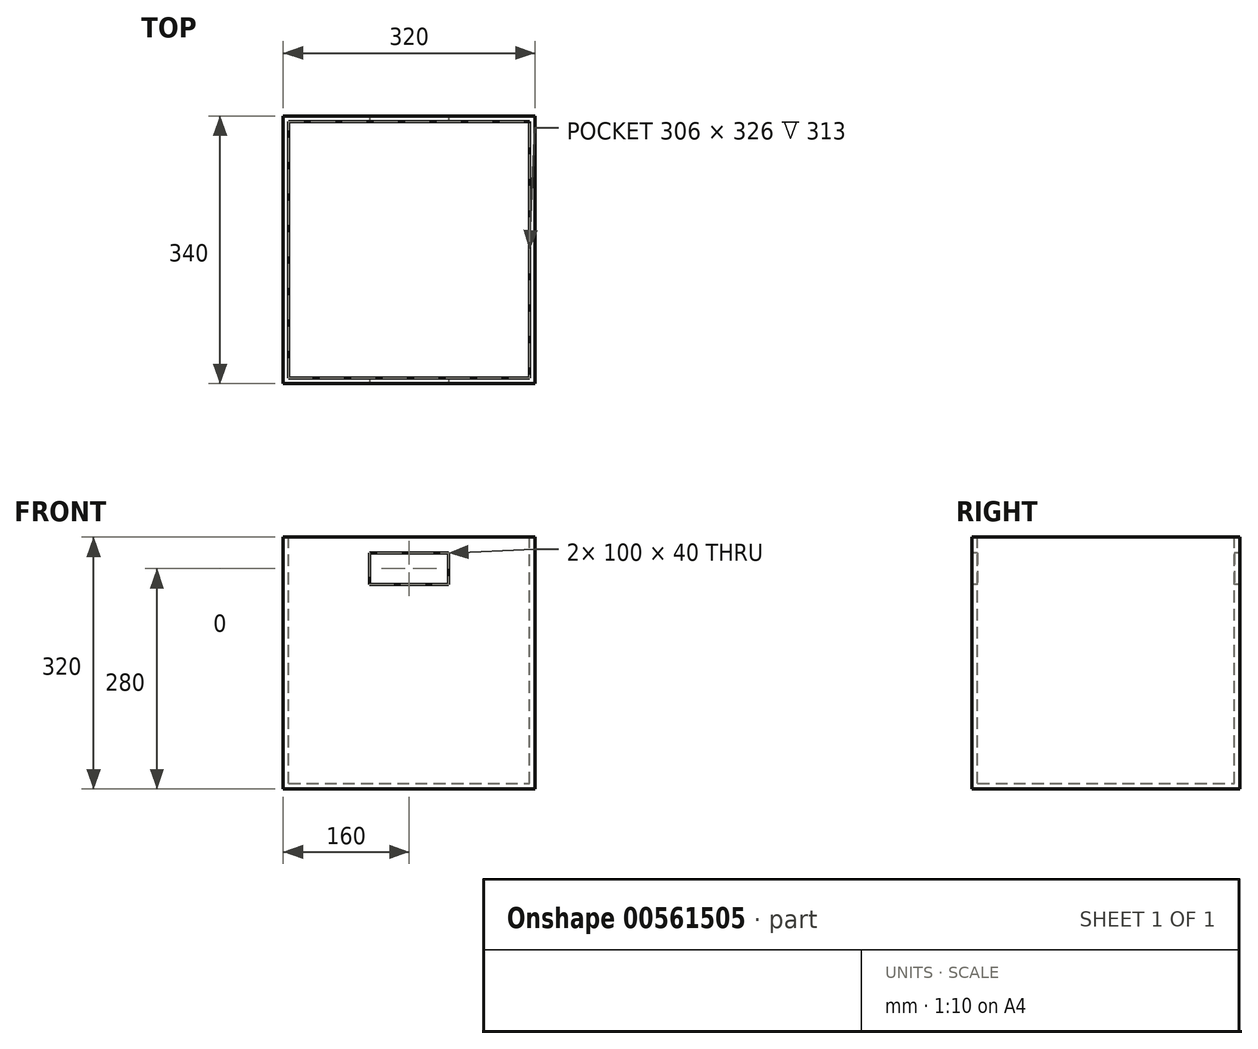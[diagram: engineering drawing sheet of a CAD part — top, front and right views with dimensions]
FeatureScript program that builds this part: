
annotation { "Feature Type Name" : "Feature", "Feature Type Description" : "" }
export const myFeature = defineFeature(function(context is Context, id is Id, definition is map)
    precondition{}
    {
        {
            var Q0;
            Q0=qCreatedBy(makeId("Front.planeOp"),FACE);
            var sketch = newSketch(context, id + "F0", { "sketchPlane" : qUnion([Q0])});
            skLineSegment(sketch, "E0.bottom", {"start": v(0, 0) * mm, "end": v(320, 0) * mm});
            skLineSegment(sketch, "E0.top", {"start": v(0, 320) * mm, "end": v(320, 320) * mm});
            skLineSegment(sketch, "E0.left", {"start": v(0, 0) * mm, "end": v(0, 320) * mm});
            skLineSegment(sketch, "E0.right", {"start": v(320, 0) * mm, "end": v(320, 320) * mm});
            skSolve(sketch);
        }
        {
            var Q0;
            Q0 = qSketchRegion(id + "F0", true);
            extrude(context, id + "F1", {"entities" : qUnion([Q0]), "depth" : 340 * mm, "offsetDistance" : 25 * mm, "symmetric" : true});
        }
        {
            var Q0;
            Q0=makeQuery(id+"F1.opExtrude","SWEPT_FACE",FACE,{"disambiguationData":[OSD([sQuery(id+"F0.wireOp",EDGE,"E0.top")])]});
            shell(context, id + "F2", {"entities" : qUnion([Q0]), "thickness" : 7 * mm});
        }
        {
            var Q0;
            Q0=makeQuery(id+"F1.opExtrude","CAP_FACE",FACE,{"disambiguationData":[OSD([sQuery(id+"F0.wireOp",EDGE,"E0.bottom"),sQuery(id+"F0.wireOp",EDGE,"E0.top"),sQuery(id+"F0.wireOp",EDGE,"E0.left"),sQuery(id+"F0.wireOp",EDGE,"E0.right")])],"isStart":false});
            var sketch = newSketch(context, id + "F3", { "sketchPlane" : qUnion([Q0])});
            skLineSegment(sketch, "E1.bottom", {"start": v(110, 300) * mm, "end": v(210, 300) * mm});
            skLineSegment(sketch, "E1.top", {"start": v(110, 260) * mm, "end": v(210, 260) * mm});
            skLineSegment(sketch, "E1.left", {"start": v(110, 300) * mm, "end": v(110, 260) * mm});
            skLineSegment(sketch, "E1.right", {"start": v(210, 300) * mm, "end": v(210, 260) * mm});
            skPoint(sketch, "E2", {"position": v(160, 300) * mm});
            skPoint(sketch, "E3", {"position": v(160, 320) * mm});
            skSolve(sketch);
        }
        {
            var Q0;
            Q0 = qSketchRegion(id + "F3", true);
            extrude(context, id + "F4", {"entities" : qUnion([Q0]), "operationType" : NewBodyOperationType.REMOVE, "endBound" : BoundingType.THROUGH_ALL, "oppositeDirection" : true, "depth" : 25 * mm, "offsetDistance" : 25 * mm});
        }
    });
